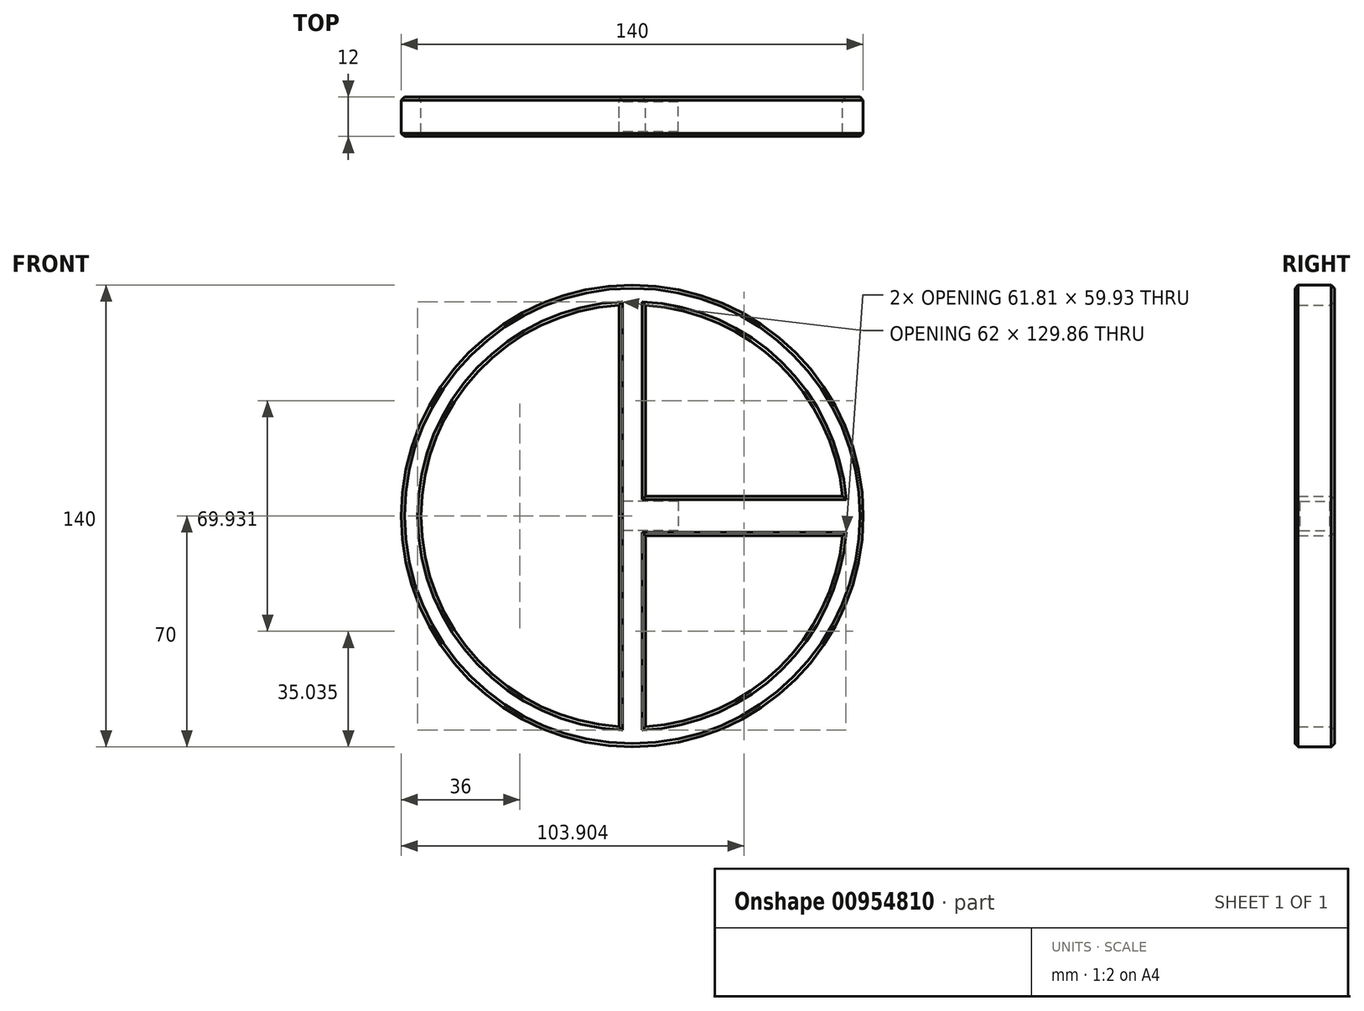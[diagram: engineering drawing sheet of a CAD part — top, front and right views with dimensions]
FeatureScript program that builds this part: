
annotation { "Feature Type Name" : "Feature", "Feature Type Description" : "" }
export const myFeature = defineFeature(function(context is Context, id is Id, definition is map)
    precondition{}
    {
        {
            var Q0;
            Q0=qCreatedBy(makeId("Front.planeOp"),FACE);
            var sketch = newSketch(context, id + "F0", { "sketchPlane" : qUnion([Q0])});
            skCircle(sketch, "E0", {"center": v(0, 0) * mm, "radius": 70 * mm});
            skCircle(sketch, "E1", {"center": v(0, 0) * mm, "radius": 64 * mm});
            skLineSegment(sketch, "E2.left", {"start": v(4, 63.87) * mm, "end": v(4, 6) * mm});
            skLineSegment(sketch, "E2.right", {"start": v(-4, 63.87) * mm, "end": v(-4, 6) * mm});
            skLineSegment(sketch, "E3.bottom", {"start": v(63.72, 6) * mm, "end": v(4, 6) * mm});
            skLineSegment(sketch, "E3.top", {"start": v(63.72, -6) * mm, "end": v(4, -6) * mm});
            skLineSegment(sketch, "E4", {"start": v(-4, 6) * mm, "end": v(-4, -6) * mm});
            skLineSegment(sketch, "E5", {"start": v(-4, -6) * mm, "end": v(-4, -63.87) * mm});
            skLineSegment(sketch, "E6", {"start": v(4, -6) * mm, "end": v(4, -63.87) * mm});
            skSolve(sketch);
        }
        {
            var Q0;
            Q0 = qSketchRegion(id + "F0", true);
            var Q1;
            {var subQ5=sQuery(id+"F0.wireOp",EDGE,"E2.left");Q1=makeQuery(id+"F0.imprint","IMPRINT",FACE,{"disambiguationData":[TD([[makeQuery(id+"F0.imprint","IMPRINT",EDGE,{"derivedFrom":subQ5}),-1.0]])]});}
            extrude(context, id + "F1", {"entities" : qUnion([Q0, Q1]), "depth" : 12 * mm, "offsetDistance" : 25 * mm});
        }
        {
            var Q0;
            Q0=makeQuery(id+"F1.opExtrude","SWEPT_FACE",FACE,{"disambiguationData":[OSD([sQuery(id+"F0.wireOp",EDGE,"E2.right"),sQuery(id+"F0.wireOp",EDGE,"E4"),sQuery(id+"F0.wireOp",EDGE,"E5")])]});
            var sketch = newSketch(context, id + "F2", { "sketchPlane" : qUnion([Q0])});
            skLineSegment(sketch, "E7.0", {"start": v(12, 6) * mm, "end": v(0, 6) * mm});
            skLineSegment(sketch, "E8.0", {"start": v(12, -6) * mm, "end": v(0, -6) * mm});
            skLineSegment(sketch, "E9", {"start": v(0, 6) * mm, "end": v(0, -6) * mm});
            skLineSegment(sketch, "E10", {"start": v(12, 6) * mm, "end": v(12, -6) * mm});
            skLineSegment(sketch, "E11.0", {"start": v(10.5, 4.5) * mm, "end": v(1.5, 4.5) * mm});
            skLineSegment(sketch, "E11.1", {"start": v(10.5, 4.5) * mm, "end": v(10.5, -4.5) * mm});
            skLineSegment(sketch, "E11.2", {"start": v(10.5, -4.5) * mm, "end": v(1.5, -4.5) * mm});
            skLineSegment(sketch, "E11.3", {"start": v(1.5, 4.5) * mm, "end": v(1.5, -4.5) * mm});
            skSolve(sketch);
        }
        {
            var Q0;
            Q0=makeQuery(id+"F2.imprint","IMPRINT",FACE,{"disambiguationData":[TD([[makeQuery(id+"F2.imprint","IMPRINT",EDGE,{"derivedFrom":sQuery(id+"F2.wireOp",EDGE,"E11.0")}),1.0]])]});
            extrude(context, id + "F3", {"entities" : qUnion([Q0]), "operationType" : NewBodyOperationType.REMOVE, "oppositeDirection" : true, "depth" : 18 * mm, "offsetDistance" : 25 * mm});
        }
        {
            var Q0;
            Q0=makeQuery(id+"F1.opExtrude","CAP_EDGE",EDGE,{"disambiguationData":[OSD([sQuery(id+"F0.wireOp",EDGE,"E3.bottom")])],"isStart":true});
            var Q1;
            Q1=makeQuery(id+"F1.opExtrude","CAP_EDGE",EDGE,{"disambiguationData":[OSD([sQuery(id+"F0.wireOp",EDGE,"E3.top")])],"isStart":true});
            var Q2;
            {var subQ0=sQuery(id+"F0.wireOp",EDGE,"E1");Q2=makeQuery(id+"F1.opExtrude","CAP_EDGE",EDGE,{"disambiguationData":[OSD([subQ0]),TDD([makeQuery(id+"F0.imprint","IMPRINT",EDGE,{"disambiguationData":[TD([[makeQuery(id+"F0.imprint","INTERSECT",VERTEX,{"derivedFrom":[subQ0,sQuery(id+"F0.wireOp",EDGE,"E2.left")]}),1.0]])],"derivedFrom":subQ0})])],"isStart":true});}
            var Q3;
            {var subQ0=sQuery(id+"F0.wireOp",EDGE,"E1");Q3=makeQuery(id+"F1.opExtrude","CAP_EDGE",EDGE,{"disambiguationData":[OSD([subQ0]),TDD([makeQuery(id+"F0.imprint","IMPRINT",EDGE,{"disambiguationData":[TD([[makeQuery(id+"F0.imprint","INTERSECT",VERTEX,{"derivedFrom":[subQ0,sQuery(id+"F0.wireOp",EDGE,"E3.top")]}),1.0]])],"derivedFrom":subQ0})])],"isStart":true});}
            var Q4;
            Q4=makeQuery(id+"F1.opExtrude","CAP_EDGE",EDGE,{"disambiguationData":[OSD([sQuery(id+"F0.wireOp",EDGE,"E6")])],"isStart":true});
            var Q5;
            Q5=makeQuery(id+"F1.opExtrude","CAP_EDGE",EDGE,{"disambiguationData":[OSD([sQuery(id+"F0.wireOp",EDGE,"E2.left")])],"isStart":true});
            var Q6;
            Q6=makeQuery(id+"F1.opExtrude","CAP_EDGE",EDGE,{"disambiguationData":[OSD([sQuery(id+"F0.wireOp",EDGE,"E2.right"),sQuery(id+"F0.wireOp",EDGE,"E4"),sQuery(id+"F0.wireOp",EDGE,"E5")])],"isStart":true});
            var Q7;
            Q7=makeQuery(id+"F3.boolean.opBoolean","COPY",EDGE,{"derivedFrom":makeQuery(id+"F3.opExtrude","CAP_EDGE",EDGE,{"disambiguationData":[OSD([sQuery(id+"F2.wireOp",EDGE,"E11.0")])],"isStart":true})});
            var Q8;
            Q8=makeQuery(id+"F3.boolean.opBoolean","COPY",EDGE,{"derivedFrom":makeQuery(id+"F3.opExtrude","CAP_EDGE",EDGE,{"disambiguationData":[OSD([sQuery(id+"F2.wireOp",EDGE,"E11.2")])],"isStart":true})});
            var Q9;
            Q9=makeQuery(id+"F3.boolean.opBoolean","COPY",EDGE,{"derivedFrom":makeQuery(id+"F3.opExtrude","CAP_EDGE",EDGE,{"disambiguationData":[OSD([sQuery(id+"F2.wireOp",EDGE,"E11.3")])],"isStart":true})});
            var Q10;
            {var subQ0=sQuery(id+"F0.wireOp",EDGE,"E1");Q10=makeQuery(id+"F1.opExtrude","CAP_EDGE",EDGE,{"disambiguationData":[OSD([subQ0]),TDD([makeQuery(id+"F0.imprint","IMPRINT",EDGE,{"disambiguationData":[TD([[makeQuery(id+"F0.imprint","INTERSECT",VERTEX,{"derivedFrom":[subQ0,sQuery(id+"F0.wireOp",EDGE,"E2.right")]}),-1.0]])],"derivedFrom":subQ0})])],"isStart":true});}
            var Q11;
            Q11=makeQuery(id+"F1.opExtrude","CAP_EDGE",EDGE,{"disambiguationData":[OSD([sQuery(id+"F0.wireOp",EDGE,"E0")])],"isStart":true});
            var Q12;
            Q12=makeQuery(id+"F1.opExtrude","CAP_EDGE",EDGE,{"disambiguationData":[OSD([sQuery(id+"F0.wireOp",EDGE,"E0")])],"isStart":false});
            var Q13;
            {var subQ0=sQuery(id+"F0.wireOp",EDGE,"E1");Q13=makeQuery(id+"F1.opExtrude","CAP_EDGE",EDGE,{"disambiguationData":[OSD([subQ0]),TDD([makeQuery(id+"F0.imprint","IMPRINT",EDGE,{"disambiguationData":[TD([[makeQuery(id+"F0.imprint","INTERSECT",VERTEX,{"derivedFrom":[subQ0,sQuery(id+"F0.wireOp",EDGE,"E2.right")]}),-1.0]])],"derivedFrom":subQ0})])],"isStart":false});}
            var Q14;
            Q14=makeQuery(id+"F1.opExtrude","CAP_EDGE",EDGE,{"disambiguationData":[OSD([sQuery(id+"F0.wireOp",EDGE,"E2.right"),sQuery(id+"F0.wireOp",EDGE,"E4"),sQuery(id+"F0.wireOp",EDGE,"E5")])],"isStart":false});
            var Q15;
            Q15=makeQuery(id+"F1.opExtrude","CAP_EDGE",EDGE,{"disambiguationData":[OSD([sQuery(id+"F0.wireOp",EDGE,"E2.left")])],"isStart":false});
            var Q16;
            Q16=makeQuery(id+"F1.opExtrude","CAP_EDGE",EDGE,{"disambiguationData":[OSD([sQuery(id+"F0.wireOp",EDGE,"E6")])],"isStart":false});
            var Q17;
            Q17=makeQuery(id+"F1.opExtrude","CAP_EDGE",EDGE,{"disambiguationData":[OSD([sQuery(id+"F0.wireOp",EDGE,"E3.top")])],"isStart":false});
            var Q18;
            Q18=makeQuery(id+"F1.opExtrude","CAP_EDGE",EDGE,{"disambiguationData":[OSD([sQuery(id+"F0.wireOp",EDGE,"E3.bottom")])],"isStart":false});
            var Q19;
            {var subQ0=sQuery(id+"F0.wireOp",EDGE,"E1");Q19=makeQuery(id+"F1.opExtrude","CAP_EDGE",EDGE,{"disambiguationData":[OSD([subQ0]),TDD([makeQuery(id+"F0.imprint","IMPRINT",EDGE,{"disambiguationData":[TD([[makeQuery(id+"F0.imprint","INTERSECT",VERTEX,{"derivedFrom":[subQ0,sQuery(id+"F0.wireOp",EDGE,"E2.left")]}),1.0]])],"derivedFrom":subQ0})])],"isStart":false});}
            var Q20;
            {var subQ0=sQuery(id+"F0.wireOp",EDGE,"E1");Q20=makeQuery(id+"F1.opExtrude","CAP_EDGE",EDGE,{"disambiguationData":[OSD([subQ0]),TDD([makeQuery(id+"F0.imprint","IMPRINT",EDGE,{"disambiguationData":[TD([[makeQuery(id+"F0.imprint","INTERSECT",VERTEX,{"derivedFrom":[subQ0,sQuery(id+"F0.wireOp",EDGE,"E3.top")]}),1.0]])],"derivedFrom":subQ0})])],"isStart":false});}
            var Q21;
            Q21=makeQuery(id+"F3.boolean.opBoolean","COPY",EDGE,{"derivedFrom":makeQuery(id+"F3.opExtrude","CAP_EDGE",EDGE,{"disambiguationData":[OSD([sQuery(id+"F2.wireOp",EDGE,"E11.1")])],"isStart":true})});
            chamfer(context, id + "F4", {"entities" : qUnion([Q0, Q1, Q2, Q3, Q4, Q5, Q6, Q7, Q8, Q9, Q10, Q11, Q12, Q13, Q14, Q15, Q16, Q17, Q18, Q19, Q20, Q21]), "width" : 1 * mm, "tangentPropagation" : true});
        }
    });
